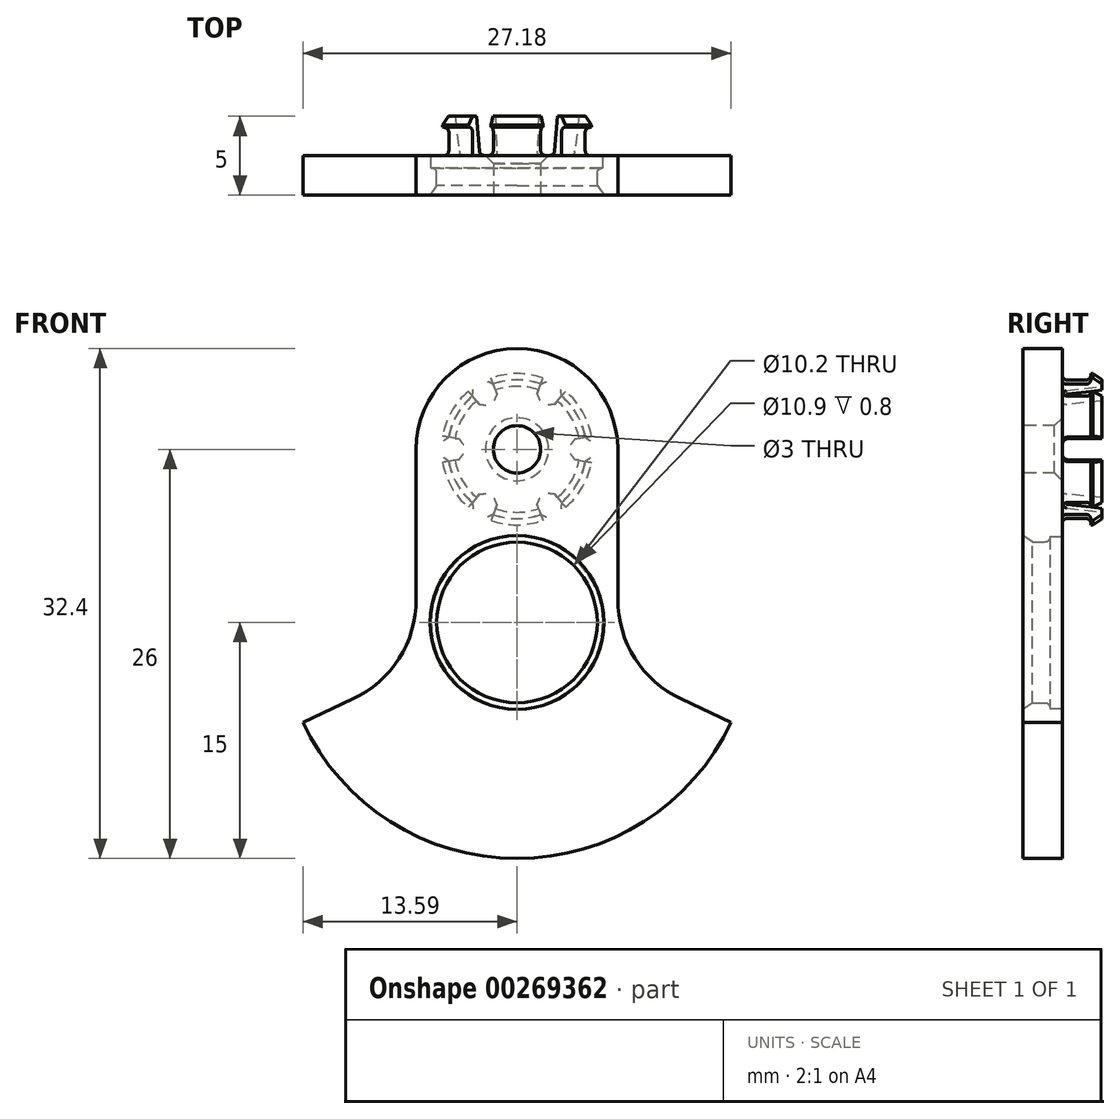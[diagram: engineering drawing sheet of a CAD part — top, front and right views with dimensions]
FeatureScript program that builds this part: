
annotation { "Feature Type Name" : "Feature", "Feature Type Description" : "" }
export const myFeature = defineFeature(function(context is Context, id is Id, definition is map)
    precondition{}
    {
        {
            var Q0;
            Q0=qCreatedBy(makeId("Front.planeOp"),FACE);
            var sketch = newSketch(context, id + "F0", { "sketchPlane" : qUnion([Q0])});
            skCircle(sketch, "E0", {"center": v(0, 0) * mm, "radius": 4.4 * mm});
            skLineSegment(sketch, "E1", {"start": v(0, 0) * mm, "end": v(0, 25.39) * mm, "construction": true});
            skCircle(sketch, "E2", {"center": v(0, -11) * mm, "radius": 5.1 * mm});
            skArc(sketch, "E3", {"start": v(-13.6, -17.34) * mm, "mid": v(0, -26) * mm, "end": v(13.6, -17.34) * mm});
            skLineSegment(sketch, "E4", {"start": v(-10.44, -15.87) * mm, "end": v(-13.6, -17.34) * mm});
            skLineSegment(sketch, "E5", {"start": v(-13.6, -17.34) * mm, "end": v(-10.44, -15.87) * mm});
            skLineSegment(sketch, "E6", {"start": v(13.6, -17.34) * mm, "end": v(10.44, -15.87) * mm});
            skLineSegment(sketch, "E7", {"start": v(-6.4, 0) * mm, "end": v(-6.4, -9.52) * mm});
            skArc(sketch, "E8", {"start": v(-10.44, -15.87) * mm, "mid": v(-7.5, -13.29) * mm, "end": v(-6.4, -9.52) * mm});
            skLineSegment(sketch, "E9", {"start": v(6.4, 0) * mm, "end": v(6.4, -9.52) * mm});
            skArc(sketch, "E10", {"start": v(6.4, -9.52) * mm, "mid": v(7.5, -13.29) * mm, "end": v(10.44, -15.87) * mm});
            skArc(sketch, "E11.trimOffspring", {"start": v(6.4, 0) * mm, "mid": v(0, 6.4) * mm, "end": v(-6.4, 0) * mm});
            skSolve(sketch);
        }
        {
            var Q0;
            Q0=makeQuery(id+"F0.imprint","IMPRINT",FACE,{"disambiguationData":[TD([[makeQuery(id+"F0.imprint","IMPRINT",EDGE,{"derivedFrom":sQuery(id+"F0.wireOp",EDGE,"E0")}),-1.0]])]});
            var Q1;
            Q1=makeQuery(id+"F0.imprint","IMPRINT",FACE,{"disambiguationData":[TD([[makeQuery(id+"F0.imprint","IMPRINT",EDGE,{"derivedFrom":sQuery(id+"F0.wireOp",EDGE,"E0")}),1.0]])]});
            extrude(context, id + "F1", {"entities" : qUnion([Q0, Q1]), "depth" : 2.5 * mm});
        }
        {
            var Q0;
            Q0=qCreatedBy(makeId("Top.planeOp"),FACE);
            cPlane(context, id + "F2", {"entities" : qUnion([Q0]), "cplaneType" : CPlaneType.OFFSET, "offset" : 11 * mm, "oppositeDirection" : true, "width" : 150 * mm, "height" : 150 * mm});
        }
        {
            var Q0;
            Q0=qCreatedBy(id+"F2.planeOp",FACE);
            var sketch = newSketch(context, id + "F3", { "sketchPlane" : qUnion([Q0])});
            skLineSegment(sketch, "E12.bottom", {"start": v(5, -0.8) * mm, "end": v(5.45, -0.8) * mm});
            skLineSegment(sketch, "E12.top", {"start": v(5, 0) * mm, "end": v(5.45, 0) * mm});
            skLineSegment(sketch, "E12.left", {"start": v(5, -0.8) * mm, "end": v(5, 0) * mm});
            skLineSegment(sketch, "E12.right", {"start": v(5.45, -0.8) * mm, "end": v(5.45, 0) * mm});
            skLineSegment(sketch, "E13", {"start": v(0, 0) * mm, "end": v(0, 6.8) * mm, "construction": true});
            skSolve(sketch);
        }
        {
            var Q0;
            Q0=makeQuery(id+"F3.imprint","IMPRINT",FACE,{"disambiguationData":[TD([[makeQuery(id+"F3.imprint","IMPRINT",EDGE,{"derivedFrom":sQuery(id+"F3.wireOp",EDGE,"E12.bottom")}),1.0]])]});
            var Q1;
            Q1=sQuery(id+"F3.wireOp",EDGE,"E13");
            revolve(context, id + "F4", {"operationType" : NewBodyOperationType.REMOVE, "entities" : qUnion([Q0]), "axis" : qUnion([Q1]), "revolveType" : RevolveType.FULL, "oppositeDirection" : true});
        }
        {
            var Q0;
            Q0=makeQuery(id+"F1.opExtrude","CAP_EDGE",EDGE,{"disambiguationData":[OSD([sQuery(id+"F0.wireOp",EDGE,"E2")])],"isStart":false});
            chamfer(context, id + "F5", {"entities" : qUnion([Q0]), "chamferType" : ChamferType.OFFSET_ANGLE, "width" : 0.6 * mm, "oppositeDirection" : false, "angle" : 35 * degree, "tangentPropagation" : true});
        }
        {
            var Q0;
            Q0=makeQuery(id+"F4.boolean.opBoolean","INTERSECT",EDGE,{"derivedFrom":[makeQuery(id+"F1.opExtrude","SWEPT_FACE",FACE,{"disambiguationData":[OSD([sQuery(id+"F0.wireOp",EDGE,"E2")])]}),makeQuery(id+"F4.opRevolve","SWEPT_FACE",FACE,{"disambiguationData":[OSD([sQuery(id+"F3.wireOp",EDGE,"E12.bottom")])]})]});
            fillet(context, id + "F6", {"entities" : qUnion([Q0]), "radius" : 0.3 * mm, "tangentPropagation" : true, "allowEdgeOverflow" : false});
        }
        {
            var Q0;
            Q0=qCreatedBy(makeId("Top.planeOp"),FACE);
            var sketch = newSketch(context, id + "F7", { "sketchPlane" : qUnion([Q0])});
            skLineSegment(sketch, "E14.bottom", {"start": v(3.5, -2.5) * mm, "end": v(4.4, -2.5) * mm});
            skLineSegment(sketch, "E14.top", {"start": v(3.5, 2.5) * mm, "end": v(4.4, 2.5) * mm});
            skLineSegment(sketch, "E14.left", {"start": v(3.5, -2.5) * mm, "end": v(3.5, 2.5) * mm});
            skLineSegment(sketch, "E14.right", {"start": v(4.4, -2.5) * mm, "end": v(4.4, 1.8) * mm});
            skLineSegment(sketch, "E15", {"start": v(0, 0) * mm, "end": v(0, 10.72) * mm, "construction": true});
            skLineSegment(sketch, "E16.bottom", {"start": v(4.4, 2.5) * mm, "end": v(4.8, 2.5) * mm});
            skLineSegment(sketch, "E16.top", {"start": v(4.4, 1.8) * mm, "end": v(4.8, 1.8) * mm});
            skLineSegment(sketch, "E16.right", {"start": v(4.8, 2.5) * mm, "end": v(4.8, 1.8) * mm});
            skSolve(sketch);
        }
        {
            var Q0;
            Q0=makeQuery(id+"F7.imprint","IMPRINT",FACE,{"disambiguationData":[TD([[makeQuery(id+"F7.imprint","IMPRINT",EDGE,{"derivedFrom":sQuery(id+"F7.wireOp",EDGE,"E14.bottom")}),1.0]])]});
            var Q1;
            Q1=sQuery(id+"F7.wireOp",EDGE,"E15");
            revolve(context, id + "F8", {"operationType" : NewBodyOperationType.ADD, "entities" : qUnion([Q0]), "axis" : qUnion([Q1]), "revolveType" : RevolveType.FULL});
        }
        {
            var Q0;
            Q0=makeQuery(id+"F8.opRevolve","SWEPT_EDGE",EDGE,{"disambiguationData":[OSD([sQuery(id+"F7.wireOp",EDGE,"E14.right"),sQuery(id+"F7.wireOp",EDGE,"E16.top")])]});
            fillet(context, id + "F9", {"entities" : qUnion([Q0]), "radius" : 0.3 * mm, "tangentPropagation" : true, "allowEdgeOverflow" : false});
        }
        {
            var Q0;
            Q0=makeQuery(id+"F8.opRevolve","SWEPT_EDGE",EDGE,{"disambiguationData":[OSD([sQuery(id+"F7.wireOp",EDGE,"E14.top"),sQuery(id+"F7.wireOp",EDGE,"E14.left")])]});
            chamfer(context, id + "F10", {"entities" : qUnion([Q0]), "chamferType" : ChamferType.TWO_OFFSETS, "width1" : 0.5 * mm, "oppositeDirection" : false, "width2" : 4 * mm, "tangentPropagation" : true});
        }
        {
            var Q0;
            Q0=makeQuery(id+"F8.opRevolve","SWEPT_EDGE",EDGE,{"disambiguationData":[OSD([sQuery(id+"F7.wireOp",EDGE,"E16.bottom"),sQuery(id+"F7.wireOp",EDGE,"E16.right")])]});
            chamfer(context, id + "F11", {"entities" : qUnion([Q0]), "chamferType" : ChamferType.OFFSET_ANGLE, "width" : 0.55 * mm, "oppositeDirection" : false, "angle" : 35 * degree, "tangentPropagation" : true});
        }
        {
            var Q0;
            Q0=qCreatedBy(makeId("Front.planeOp"),FACE);
            var sketch = newSketch(context, id + "F12", { "sketchPlane" : qUnion([Q0])});
            skCircle(sketch, "E17", {"center": v(0, 0) * mm, "radius": 7.5 * mm});
            skLineSegment(sketch, "E18", {"start": v(0, 0) * mm, "end": v(0, 10.84) * mm, "construction": true});
            skLineSegment(sketch, "E19", {"start": v(0, 0) * mm, "end": v(-10.38, 0) * mm, "construction": true});
            skLineSegment(sketch, "E20", {"start": v(0, 0) * mm, "end": v(-2.57, 7.05) * mm});
            skLineSegment(sketch, "E21", {"start": v(0, 0) * mm, "end": v(-4.82, 5.75) * mm});
            skLineSegment(sketch, "E22.1.0", {"start": v(0, 0) * mm, "end": v(-7.39, 1.3) * mm});
            skLineSegment(sketch, "E22.1.1", {"start": v(0, 0) * mm, "end": v(-7.39, -1.3) * mm});
            skLineSegment(sketch, "E22.2.0", {"start": v(0, 0) * mm, "end": v(-4.82, -5.75) * mm});
            skLineSegment(sketch, "E22.2.1", {"start": v(0, 0) * mm, "end": v(-2.57, -7.05) * mm});
            skLineSegment(sketch, "E22.3.0", {"start": v(0, 0) * mm, "end": v(2.57, -7.05) * mm});
            skLineSegment(sketch, "E22.3.1", {"start": v(0, 0) * mm, "end": v(4.82, -5.75) * mm});
            skLineSegment(sketch, "E22.4.0", {"start": v(0, 0) * mm, "end": v(7.39, -1.3) * mm});
            skLineSegment(sketch, "E22.4.1", {"start": v(0, 0) * mm, "end": v(7.39, 1.3) * mm});
            skLineSegment(sketch, "E22.5.0", {"start": v(0, 0) * mm, "end": v(4.82, 5.75) * mm});
            skLineSegment(sketch, "E22.5.1", {"start": v(0, 0) * mm, "end": v(2.57, 7.05) * mm});
            skSolve(sketch);
        }
        {
            var Q0;
            {var subQ0=sQuery(id+"F12.wireOp",EDGE,"E22.5.0");Q0=makeQuery(id+"F12.imprint","IMPRINT",FACE,{"disambiguationData":[TD([[makeQuery(id+"F12.imprint","IMPRINT",EDGE,{"derivedFrom":subQ0}),1.0]])]});}
            var Q1;
            {var subQ0=sQuery(id+"F12.wireOp",EDGE,"E20");Q1=makeQuery(id+"F12.imprint","IMPRINT",FACE,{"disambiguationData":[TD([[makeQuery(id+"F12.imprint","IMPRINT",EDGE,{"derivedFrom":subQ0}),1.0]])]});}
            var Q2;
            {var subQ0=sQuery(id+"F12.wireOp",EDGE,"E22.4.0");Q2=makeQuery(id+"F12.imprint","IMPRINT",FACE,{"disambiguationData":[TD([[makeQuery(id+"F12.imprint","IMPRINT",EDGE,{"derivedFrom":subQ0}),1.0]])]});}
            var Q3;
            {var subQ0=sQuery(id+"F12.wireOp",EDGE,"E22.3.0");Q3=makeQuery(id+"F12.imprint","IMPRINT",FACE,{"disambiguationData":[TD([[makeQuery(id+"F12.imprint","IMPRINT",EDGE,{"derivedFrom":subQ0}),1.0]])]});}
            var Q4;
            {var subQ0=sQuery(id+"F12.wireOp",EDGE,"E22.2.0");Q4=makeQuery(id+"F12.imprint","IMPRINT",FACE,{"disambiguationData":[TD([[makeQuery(id+"F12.imprint","IMPRINT",EDGE,{"derivedFrom":subQ0}),1.0]])]});}
            var Q5;
            {var subQ0=sQuery(id+"F12.wireOp",EDGE,"E22.1.0");Q5=makeQuery(id+"F12.imprint","IMPRINT",FACE,{"disambiguationData":[TD([[makeQuery(id+"F12.imprint","IMPRINT",EDGE,{"derivedFrom":subQ0}),1.0]])]});}
            extrude(context, id + "F13", {"entities" : qUnion([Q0, Q1, Q2, Q3, Q4, Q5]), "operationType" : NewBodyOperationType.REMOVE, "endBound" : BoundingType.THROUGH_ALL, "oppositeDirection" : true, "depth" : 25 * mm});
        }
        {
            var Q0;
            Q0=makeQuery(id+"F13.boolean.opBoolean","COPY",EDGE,{"derivedFrom":makeQuery(id+"F13.opExtrude","CAP_EDGE",EDGE,{"disambiguationData":[OSD([sQuery(id+"F12.wireOp",EDGE,"E22.4.1")])],"isStart":true})});
            var Q1;
            Q1=makeQuery(id+"F13.boolean.opBoolean","COPY",EDGE,{"derivedFrom":makeQuery(id+"F13.opExtrude","CAP_EDGE",EDGE,{"disambiguationData":[OSD([sQuery(id+"F12.wireOp",EDGE,"E22.4.0")])],"isStart":true})});
            var Q2;
            Q2=makeQuery(id+"F13.boolean.opBoolean","COPY",EDGE,{"derivedFrom":makeQuery(id+"F13.opExtrude","CAP_EDGE",EDGE,{"disambiguationData":[OSD([sQuery(id+"F12.wireOp",EDGE,"E22.5.0")])],"isStart":true})});
            var Q3;
            Q3=makeQuery(id+"F13.boolean.opBoolean","COPY",EDGE,{"derivedFrom":makeQuery(id+"F13.opExtrude","CAP_EDGE",EDGE,{"disambiguationData":[OSD([sQuery(id+"F12.wireOp",EDGE,"E22.5.1")])],"isStart":true})});
            var Q4;
            Q4=makeQuery(id+"F13.boolean.opBoolean","COPY",EDGE,{"derivedFrom":makeQuery(id+"F13.opExtrude","CAP_EDGE",EDGE,{"disambiguationData":[OSD([sQuery(id+"F12.wireOp",EDGE,"E20")])],"isStart":true})});
            var Q5;
            Q5=makeQuery(id+"F13.boolean.opBoolean","COPY",EDGE,{"derivedFrom":makeQuery(id+"F13.opExtrude","CAP_EDGE",EDGE,{"disambiguationData":[OSD([sQuery(id+"F12.wireOp",EDGE,"E21")])],"isStart":true})});
            var Q6;
            Q6=makeQuery(id+"F13.boolean.opBoolean","COPY",EDGE,{"derivedFrom":makeQuery(id+"F13.opExtrude","CAP_EDGE",EDGE,{"disambiguationData":[OSD([sQuery(id+"F12.wireOp",EDGE,"E22.1.0")])],"isStart":true})});
            var Q7;
            Q7=makeQuery(id+"F13.boolean.opBoolean","COPY",EDGE,{"derivedFrom":makeQuery(id+"F13.opExtrude","CAP_EDGE",EDGE,{"disambiguationData":[OSD([sQuery(id+"F12.wireOp",EDGE,"E22.1.1")])],"isStart":true})});
            var Q8;
            Q8=makeQuery(id+"F13.boolean.opBoolean","COPY",EDGE,{"derivedFrom":makeQuery(id+"F13.opExtrude","CAP_EDGE",EDGE,{"disambiguationData":[OSD([sQuery(id+"F12.wireOp",EDGE,"E22.2.0")])],"isStart":true})});
            var Q9;
            Q9=makeQuery(id+"F13.boolean.opBoolean","COPY",EDGE,{"derivedFrom":makeQuery(id+"F13.opExtrude","CAP_EDGE",EDGE,{"disambiguationData":[OSD([sQuery(id+"F12.wireOp",EDGE,"E22.2.1")])],"isStart":true})});
            var Q10;
            Q10=makeQuery(id+"F13.boolean.opBoolean","COPY",EDGE,{"derivedFrom":makeQuery(id+"F13.opExtrude","CAP_EDGE",EDGE,{"disambiguationData":[OSD([sQuery(id+"F12.wireOp",EDGE,"E22.3.0")])],"isStart":true})});
            var Q11;
            Q11=makeQuery(id+"F13.boolean.opBoolean","COPY",EDGE,{"derivedFrom":makeQuery(id+"F13.opExtrude","CAP_EDGE",EDGE,{"disambiguationData":[OSD([sQuery(id+"F12.wireOp",EDGE,"E22.3.1")])],"isStart":true})});
            var Q12;
            {var subQ1=makeQuery(id+"F1.opExtrude","CAP_FACE",FACE,{"disambiguationData":[OSD([sQuery(id+"F0.wireOp",EDGE,"E2"),sQuery(id+"F0.wireOp",EDGE,"E3"),sQuery(id+"F0.wireOp",EDGE,"E5"),sQuery(id+"F0.wireOp",EDGE,"E6"),sQuery(id+"F0.wireOp",EDGE,"E7"),sQuery(id+"F0.wireOp",EDGE,"E8"),sQuery(id+"F0.wireOp",EDGE,"E9"),sQuery(id+"F0.wireOp",EDGE,"E10"),sQuery(id+"F0.wireOp",EDGE,"E11.trimOffspring")])],"isStart":true});var subQ2=makeQuery(id+"F8.opRevolve","SWEPT_FACE",FACE,{"disambiguationData":[OSD([sQuery(id+"F7.wireOp",EDGE,"E14.right")])]});var subQ3=sQuery(id+"F12.wireOp",EDGE,"E22.3.1");Q12=makeQuery(id+"F13.boolean.opBoolean","SPLIT",EDGE,{"disambiguationData":[TD([makeQuery(id+"F13.opExtrude","SWEPT_FACE",FACE,{"disambiguationData":[OSD([subQ3])]})])],"derivedFrom":makeQuery(id+"F8.boolean.opBoolean","INTERSECT",EDGE,{"derivedFrom":[subQ1,subQ2]})});}
            var Q13;
            {var subQ1=sQuery(id+"F7.wireOp",EDGE,"E14.left");var subQ2=sQuery(id+"F7.wireOp",EDGE,"E14.top");var subQ3=makeQuery(id+"F1.opExtrude","CAP_FACE",FACE,{"disambiguationData":[OSD([sQuery(id+"F0.wireOp",EDGE,"E2"),sQuery(id+"F0.wireOp",EDGE,"E3"),sQuery(id+"F0.wireOp",EDGE,"E5"),sQuery(id+"F0.wireOp",EDGE,"E6"),sQuery(id+"F0.wireOp",EDGE,"E7"),sQuery(id+"F0.wireOp",EDGE,"E8"),sQuery(id+"F0.wireOp",EDGE,"E9"),sQuery(id+"F0.wireOp",EDGE,"E10"),sQuery(id+"F0.wireOp",EDGE,"E11.trimOffspring")])],"isStart":true});var subQ4=sQuery(id+"F12.wireOp",EDGE,"E22.3.1");Q13=makeQuery(id+"F13.boolean.opBoolean","SPLIT",EDGE,{"disambiguationData":[TD([makeQuery(id+"F13.opExtrude","SWEPT_FACE",FACE,{"disambiguationData":[OSD([subQ4])]})])],"derivedFrom":makeQuery(id+"F10.opChamfer","BLEND_EDGE",EDGE,{"blendedFrom":[makeQuery(id+"F8.opRevolve","SWEPT_EDGE",EDGE,{"disambiguationData":[OSD([subQ2,subQ1])]}),makeQuery(id+"F8.boolean.opBoolean","SPLIT",FACE,{"disambiguationData":[TD([makeQuery(id+"F8.opRevolve","SWEPT_FACE",FACE,{"disambiguationData":[OSD([subQ1])]})])],"derivedFrom":subQ3})],"blendedInto":[makeQuery(id+"F8.boolean.opBoolean","SPLIT",FACE,{"disambiguationData":[TD([makeQuery(id+"F8.opRevolve","SWEPT_FACE",FACE,{"disambiguationData":[OSD([subQ1])]})])],"derivedFrom":subQ3})]})});}
            var Q14;
            {var subQ1=sQuery(id+"F7.wireOp",EDGE,"E14.left");var subQ2=sQuery(id+"F7.wireOp",EDGE,"E14.top");var subQ4=makeQuery(id+"F1.opExtrude","CAP_FACE",FACE,{"disambiguationData":[OSD([sQuery(id+"F0.wireOp",EDGE,"E2"),sQuery(id+"F0.wireOp",EDGE,"E3"),sQuery(id+"F0.wireOp",EDGE,"E5"),sQuery(id+"F0.wireOp",EDGE,"E6"),sQuery(id+"F0.wireOp",EDGE,"E7"),sQuery(id+"F0.wireOp",EDGE,"E8"),sQuery(id+"F0.wireOp",EDGE,"E9"),sQuery(id+"F0.wireOp",EDGE,"E10"),sQuery(id+"F0.wireOp",EDGE,"E11.trimOffspring")])],"isStart":true});var subQ5=sQuery(id+"F12.wireOp",EDGE,"E22.4.1");Q14=makeQuery(id+"F13.boolean.opBoolean","SPLIT",EDGE,{"disambiguationData":[TD([makeQuery(id+"F13.opExtrude","SWEPT_FACE",FACE,{"disambiguationData":[OSD([subQ5])]})])],"derivedFrom":makeQuery(id+"F10.opChamfer","BLEND_EDGE",EDGE,{"blendedFrom":[makeQuery(id+"F8.opRevolve","SWEPT_EDGE",EDGE,{"disambiguationData":[OSD([subQ2,subQ1])]}),makeQuery(id+"F8.boolean.opBoolean","SPLIT",FACE,{"disambiguationData":[TD([makeQuery(id+"F8.opRevolve","SWEPT_FACE",FACE,{"disambiguationData":[OSD([subQ1])]})])],"derivedFrom":subQ4})],"blendedInto":[makeQuery(id+"F8.boolean.opBoolean","SPLIT",FACE,{"disambiguationData":[TD([makeQuery(id+"F8.opRevolve","SWEPT_FACE",FACE,{"disambiguationData":[OSD([subQ1])]})])],"derivedFrom":subQ4})]})});}
            var Q15;
            {var subQ0=sQuery(id+"F12.wireOp",EDGE,"E20");var subQ2=sQuery(id+"F7.wireOp",EDGE,"E14.left");var subQ3=sQuery(id+"F7.wireOp",EDGE,"E14.top");var subQ5=makeQuery(id+"F1.opExtrude","CAP_FACE",FACE,{"disambiguationData":[OSD([sQuery(id+"F0.wireOp",EDGE,"E2"),sQuery(id+"F0.wireOp",EDGE,"E3"),sQuery(id+"F0.wireOp",EDGE,"E5"),sQuery(id+"F0.wireOp",EDGE,"E6"),sQuery(id+"F0.wireOp",EDGE,"E7"),sQuery(id+"F0.wireOp",EDGE,"E8"),sQuery(id+"F0.wireOp",EDGE,"E9"),sQuery(id+"F0.wireOp",EDGE,"E10"),sQuery(id+"F0.wireOp",EDGE,"E11.trimOffspring")])],"isStart":true});Q15=makeQuery(id+"F13.boolean.opBoolean","SPLIT",EDGE,{"disambiguationData":[TD([makeQuery(id+"F13.opExtrude","SWEPT_FACE",FACE,{"disambiguationData":[OSD([subQ0])]})])],"derivedFrom":makeQuery(id+"F10.opChamfer","BLEND_EDGE",EDGE,{"blendedFrom":[makeQuery(id+"F8.opRevolve","SWEPT_EDGE",EDGE,{"disambiguationData":[OSD([subQ3,subQ2])]}),makeQuery(id+"F8.boolean.opBoolean","SPLIT",FACE,{"disambiguationData":[TD([makeQuery(id+"F8.opRevolve","SWEPT_FACE",FACE,{"disambiguationData":[OSD([subQ2])]})])],"derivedFrom":subQ5})],"blendedInto":[makeQuery(id+"F8.boolean.opBoolean","SPLIT",FACE,{"disambiguationData":[TD([makeQuery(id+"F8.opRevolve","SWEPT_FACE",FACE,{"disambiguationData":[OSD([subQ2])]})])],"derivedFrom":subQ5})]})});}
            var Q16;
            {var subQ0=sQuery(id+"F12.wireOp",EDGE,"E21");var subQ2=sQuery(id+"F7.wireOp",EDGE,"E14.left");var subQ3=sQuery(id+"F7.wireOp",EDGE,"E14.top");var subQ4=makeQuery(id+"F1.opExtrude","CAP_FACE",FACE,{"disambiguationData":[OSD([sQuery(id+"F0.wireOp",EDGE,"E2"),sQuery(id+"F0.wireOp",EDGE,"E3"),sQuery(id+"F0.wireOp",EDGE,"E5"),sQuery(id+"F0.wireOp",EDGE,"E6"),sQuery(id+"F0.wireOp",EDGE,"E7"),sQuery(id+"F0.wireOp",EDGE,"E8"),sQuery(id+"F0.wireOp",EDGE,"E9"),sQuery(id+"F0.wireOp",EDGE,"E10"),sQuery(id+"F0.wireOp",EDGE,"E11.trimOffspring")])],"isStart":true});Q16=makeQuery(id+"F13.boolean.opBoolean","SPLIT",EDGE,{"disambiguationData":[TD([makeQuery(id+"F13.opExtrude","SWEPT_FACE",FACE,{"disambiguationData":[OSD([subQ0])]})])],"derivedFrom":makeQuery(id+"F10.opChamfer","BLEND_EDGE",EDGE,{"blendedFrom":[makeQuery(id+"F8.opRevolve","SWEPT_EDGE",EDGE,{"disambiguationData":[OSD([subQ3,subQ2])]}),makeQuery(id+"F8.boolean.opBoolean","SPLIT",FACE,{"disambiguationData":[TD([makeQuery(id+"F8.opRevolve","SWEPT_FACE",FACE,{"disambiguationData":[OSD([subQ2])]})])],"derivedFrom":subQ4})],"blendedInto":[makeQuery(id+"F8.boolean.opBoolean","SPLIT",FACE,{"disambiguationData":[TD([makeQuery(id+"F8.opRevolve","SWEPT_FACE",FACE,{"disambiguationData":[OSD([subQ2])]})])],"derivedFrom":subQ4})]})});}
            var Q17;
            {var subQ1=sQuery(id+"F7.wireOp",EDGE,"E14.left");var subQ2=sQuery(id+"F7.wireOp",EDGE,"E14.top");var subQ3=makeQuery(id+"F1.opExtrude","CAP_FACE",FACE,{"disambiguationData":[OSD([sQuery(id+"F0.wireOp",EDGE,"E2"),sQuery(id+"F0.wireOp",EDGE,"E3"),sQuery(id+"F0.wireOp",EDGE,"E5"),sQuery(id+"F0.wireOp",EDGE,"E6"),sQuery(id+"F0.wireOp",EDGE,"E7"),sQuery(id+"F0.wireOp",EDGE,"E8"),sQuery(id+"F0.wireOp",EDGE,"E9"),sQuery(id+"F0.wireOp",EDGE,"E10"),sQuery(id+"F0.wireOp",EDGE,"E11.trimOffspring")])],"isStart":true});var subQ5=sQuery(id+"F12.wireOp",EDGE,"E22.1.1");Q17=makeQuery(id+"F13.boolean.opBoolean","SPLIT",EDGE,{"disambiguationData":[TD([makeQuery(id+"F13.opExtrude","SWEPT_FACE",FACE,{"disambiguationData":[OSD([subQ5])]})])],"derivedFrom":makeQuery(id+"F10.opChamfer","BLEND_EDGE",EDGE,{"blendedFrom":[makeQuery(id+"F8.opRevolve","SWEPT_EDGE",EDGE,{"disambiguationData":[OSD([subQ2,subQ1])]}),makeQuery(id+"F8.boolean.opBoolean","SPLIT",FACE,{"disambiguationData":[TD([makeQuery(id+"F8.opRevolve","SWEPT_FACE",FACE,{"disambiguationData":[OSD([subQ1])]})])],"derivedFrom":subQ3})],"blendedInto":[makeQuery(id+"F8.boolean.opBoolean","SPLIT",FACE,{"disambiguationData":[TD([makeQuery(id+"F8.opRevolve","SWEPT_FACE",FACE,{"disambiguationData":[OSD([subQ1])]})])],"derivedFrom":subQ3})]})});}
            var Q18;
            {var subQ1=sQuery(id+"F7.wireOp",EDGE,"E14.left");var subQ2=sQuery(id+"F7.wireOp",EDGE,"E14.top");var subQ3=makeQuery(id+"F1.opExtrude","CAP_FACE",FACE,{"disambiguationData":[OSD([sQuery(id+"F0.wireOp",EDGE,"E2"),sQuery(id+"F0.wireOp",EDGE,"E3"),sQuery(id+"F0.wireOp",EDGE,"E5"),sQuery(id+"F0.wireOp",EDGE,"E6"),sQuery(id+"F0.wireOp",EDGE,"E7"),sQuery(id+"F0.wireOp",EDGE,"E8"),sQuery(id+"F0.wireOp",EDGE,"E9"),sQuery(id+"F0.wireOp",EDGE,"E10"),sQuery(id+"F0.wireOp",EDGE,"E11.trimOffspring")])],"isStart":true});var subQ4=sQuery(id+"F12.wireOp",EDGE,"E22.2.1");Q18=makeQuery(id+"F13.boolean.opBoolean","SPLIT",EDGE,{"disambiguationData":[TD([makeQuery(id+"F13.opExtrude","SWEPT_FACE",FACE,{"disambiguationData":[OSD([subQ4])]})])],"derivedFrom":makeQuery(id+"F10.opChamfer","BLEND_EDGE",EDGE,{"blendedFrom":[makeQuery(id+"F8.opRevolve","SWEPT_EDGE",EDGE,{"disambiguationData":[OSD([subQ2,subQ1])]}),makeQuery(id+"F8.boolean.opBoolean","SPLIT",FACE,{"disambiguationData":[TD([makeQuery(id+"F8.opRevolve","SWEPT_FACE",FACE,{"disambiguationData":[OSD([subQ1])]})])],"derivedFrom":subQ3})],"blendedInto":[makeQuery(id+"F8.boolean.opBoolean","SPLIT",FACE,{"disambiguationData":[TD([makeQuery(id+"F8.opRevolve","SWEPT_FACE",FACE,{"disambiguationData":[OSD([subQ1])]})])],"derivedFrom":subQ3})]})});}
            var Q19;
            {var subQ1=makeQuery(id+"F1.opExtrude","CAP_FACE",FACE,{"disambiguationData":[OSD([sQuery(id+"F0.wireOp",EDGE,"E2"),sQuery(id+"F0.wireOp",EDGE,"E3"),sQuery(id+"F0.wireOp",EDGE,"E5"),sQuery(id+"F0.wireOp",EDGE,"E6"),sQuery(id+"F0.wireOp",EDGE,"E7"),sQuery(id+"F0.wireOp",EDGE,"E8"),sQuery(id+"F0.wireOp",EDGE,"E9"),sQuery(id+"F0.wireOp",EDGE,"E10"),sQuery(id+"F0.wireOp",EDGE,"E11.trimOffspring")])],"isStart":true});var subQ2=sQuery(id+"F12.wireOp",EDGE,"E22.2.1");var subQ3=makeQuery(id+"F8.opRevolve","SWEPT_FACE",FACE,{"disambiguationData":[OSD([sQuery(id+"F7.wireOp",EDGE,"E14.right")])]});Q19=makeQuery(id+"F13.boolean.opBoolean","SPLIT",EDGE,{"disambiguationData":[TD([makeQuery(id+"F13.opExtrude","SWEPT_FACE",FACE,{"disambiguationData":[OSD([subQ2])]})])],"derivedFrom":makeQuery(id+"F8.boolean.opBoolean","INTERSECT",EDGE,{"derivedFrom":[subQ1,subQ3]})});}
            var Q20;
            {var subQ1=makeQuery(id+"F1.opExtrude","CAP_FACE",FACE,{"disambiguationData":[OSD([sQuery(id+"F0.wireOp",EDGE,"E2"),sQuery(id+"F0.wireOp",EDGE,"E3"),sQuery(id+"F0.wireOp",EDGE,"E5"),sQuery(id+"F0.wireOp",EDGE,"E6"),sQuery(id+"F0.wireOp",EDGE,"E7"),sQuery(id+"F0.wireOp",EDGE,"E8"),sQuery(id+"F0.wireOp",EDGE,"E9"),sQuery(id+"F0.wireOp",EDGE,"E10"),sQuery(id+"F0.wireOp",EDGE,"E11.trimOffspring")])],"isStart":true});var subQ3=makeQuery(id+"F8.opRevolve","SWEPT_FACE",FACE,{"disambiguationData":[OSD([sQuery(id+"F7.wireOp",EDGE,"E14.right")])]});var subQ4=sQuery(id+"F12.wireOp",EDGE,"E22.1.1");Q20=makeQuery(id+"F13.boolean.opBoolean","SPLIT",EDGE,{"disambiguationData":[TD([makeQuery(id+"F13.opExtrude","SWEPT_FACE",FACE,{"disambiguationData":[OSD([subQ4])]})])],"derivedFrom":makeQuery(id+"F8.boolean.opBoolean","INTERSECT",EDGE,{"derivedFrom":[subQ1,subQ3]})});}
            var Q21;
            {var subQ1=makeQuery(id+"F1.opExtrude","CAP_FACE",FACE,{"disambiguationData":[OSD([sQuery(id+"F0.wireOp",EDGE,"E2"),sQuery(id+"F0.wireOp",EDGE,"E3"),sQuery(id+"F0.wireOp",EDGE,"E5"),sQuery(id+"F0.wireOp",EDGE,"E6"),sQuery(id+"F0.wireOp",EDGE,"E7"),sQuery(id+"F0.wireOp",EDGE,"E8"),sQuery(id+"F0.wireOp",EDGE,"E9"),sQuery(id+"F0.wireOp",EDGE,"E10"),sQuery(id+"F0.wireOp",EDGE,"E11.trimOffspring")])],"isStart":true});var subQ2=sQuery(id+"F12.wireOp",EDGE,"E21");var subQ3=makeQuery(id+"F8.opRevolve","SWEPT_FACE",FACE,{"disambiguationData":[OSD([sQuery(id+"F7.wireOp",EDGE,"E14.right")])]});Q21=makeQuery(id+"F13.boolean.opBoolean","SPLIT",EDGE,{"disambiguationData":[TD([makeQuery(id+"F13.opExtrude","SWEPT_FACE",FACE,{"disambiguationData":[OSD([subQ2])]})])],"derivedFrom":makeQuery(id+"F8.boolean.opBoolean","INTERSECT",EDGE,{"derivedFrom":[subQ1,subQ3]})});}
            var Q22;
            {var subQ2=makeQuery(id+"F1.opExtrude","CAP_FACE",FACE,{"disambiguationData":[OSD([sQuery(id+"F0.wireOp",EDGE,"E2"),sQuery(id+"F0.wireOp",EDGE,"E3"),sQuery(id+"F0.wireOp",EDGE,"E5"),sQuery(id+"F0.wireOp",EDGE,"E6"),sQuery(id+"F0.wireOp",EDGE,"E7"),sQuery(id+"F0.wireOp",EDGE,"E8"),sQuery(id+"F0.wireOp",EDGE,"E9"),sQuery(id+"F0.wireOp",EDGE,"E10"),sQuery(id+"F0.wireOp",EDGE,"E11.trimOffspring")])],"isStart":true});var subQ3=sQuery(id+"F12.wireOp",EDGE,"E20");var subQ4=makeQuery(id+"F8.opRevolve","SWEPT_FACE",FACE,{"disambiguationData":[OSD([sQuery(id+"F7.wireOp",EDGE,"E14.right")])]});Q22=makeQuery(id+"F13.boolean.opBoolean","SPLIT",EDGE,{"disambiguationData":[TD([makeQuery(id+"F13.opExtrude","SWEPT_FACE",FACE,{"disambiguationData":[OSD([subQ3])]})])],"derivedFrom":makeQuery(id+"F8.boolean.opBoolean","INTERSECT",EDGE,{"derivedFrom":[subQ2,subQ4]})});}
            var Q23;
            {var subQ2=makeQuery(id+"F1.opExtrude","CAP_FACE",FACE,{"disambiguationData":[OSD([sQuery(id+"F0.wireOp",EDGE,"E2"),sQuery(id+"F0.wireOp",EDGE,"E3"),sQuery(id+"F0.wireOp",EDGE,"E5"),sQuery(id+"F0.wireOp",EDGE,"E6"),sQuery(id+"F0.wireOp",EDGE,"E7"),sQuery(id+"F0.wireOp",EDGE,"E8"),sQuery(id+"F0.wireOp",EDGE,"E9"),sQuery(id+"F0.wireOp",EDGE,"E10"),sQuery(id+"F0.wireOp",EDGE,"E11.trimOffspring")])],"isStart":true});var subQ3=makeQuery(id+"F8.opRevolve","SWEPT_FACE",FACE,{"disambiguationData":[OSD([sQuery(id+"F7.wireOp",EDGE,"E14.right")])]});var subQ4=sQuery(id+"F12.wireOp",EDGE,"E22.4.1");Q23=makeQuery(id+"F13.boolean.opBoolean","SPLIT",EDGE,{"disambiguationData":[TD([makeQuery(id+"F13.opExtrude","SWEPT_FACE",FACE,{"disambiguationData":[OSD([subQ4])]})])],"derivedFrom":makeQuery(id+"F8.boolean.opBoolean","INTERSECT",EDGE,{"derivedFrom":[subQ2,subQ3]})});}
            fillet(context, id + "F14", {"entities" : qUnion([Q0, Q1, Q2, Q3, Q4, Q5, Q6, Q7, Q8, Q9, Q10, Q11, Q12, Q13, Q14, Q15, Q16, Q17, Q18, Q19, Q20, Q21, Q22, Q23]), "radius" : 0.3 * mm, "tangentPropagation" : true, "allowEdgeOverflow" : false});
        }
        {
            var Q0;
            Q0=qCreatedBy(makeId("Top.planeOp"),FACE);
            var sketch = newSketch(context, id + "F15", { "sketchPlane" : qUnion([Q0])});
            skLineSegment(sketch, "E23", {"start": v(0, -2) * mm, "end": v(0, 59.52) * mm, "construction": true});
            skLineSegment(sketch, "E24.bottom", {"start": v(0, -2) * mm, "end": v(1.5, -2) * mm});
            skLineSegment(sketch, "E24.top", {"start": v(0, 8) * mm, "end": v(1.5, 8) * mm});
            skLineSegment(sketch, "E24.left", {"start": v(0, -2) * mm, "end": v(0, 8) * mm});
            skLineSegment(sketch, "E24.right", {"start": v(1.5, -2) * mm, "end": v(1.5, 8) * mm});
            skSolve(sketch);
        }
        {
            var Q0;
            Q0=qCreatedBy(makeId("Top.planeOp"),FACE);
            var sketch = newSketch(context, id + "F16", { "sketchPlane" : qUnion([Q0])});
            skLineSegment(sketch, "E25.bottom", {"start": v(0, 10) * mm, "end": v(1.5, 10) * mm});
            skLineSegment(sketch, "E25.top", {"start": v(0, -10) * mm, "end": v(1.5, -10) * mm});
            skLineSegment(sketch, "E25.left", {"start": v(0, 10) * mm, "end": v(0, -10) * mm});
            skLineSegment(sketch, "E25.right", {"start": v(1.5, 10) * mm, "end": v(1.5, -10) * mm});
            skSolve(sketch);
        }
        {
            var Q0;
            Q0=makeQuery(id+"F16.imprint","IMPRINT",FACE,{"disambiguationData":[TD([[makeQuery(id+"F16.imprint","IMPRINT",EDGE,{"derivedFrom":sQuery(id+"F16.wireOp",EDGE,"E25.bottom")}),-1.0]])]});
            var Q1;
            Q1=sQuery(id+"F16.wireOp",EDGE,"E25.left");
            revolve(context, id + "F17", {"operationType" : NewBodyOperationType.REMOVE, "entities" : qUnion([Q0]), "axis" : qUnion([Q1]), "revolveType" : RevolveType.FULL, "oppositeDirection" : true});
        }
        {
            var Q0;
            {var subQ0=sQuery(id+"F12.wireOp",EDGE,"E17");var subQ1=sQuery(id+"F0.wireOp",EDGE,"E11.trimOffspring");var subQ2=sQuery(id+"F0.wireOp",EDGE,"E10");var subQ3=sQuery(id+"F0.wireOp",EDGE,"E9");var subQ4=sQuery(id+"F0.wireOp",EDGE,"E8");var subQ5=sQuery(id+"F0.wireOp",EDGE,"E7");var subQ6=sQuery(id+"F0.wireOp",EDGE,"E6");var subQ7=sQuery(id+"F0.wireOp",EDGE,"E5");var subQ8=sQuery(id+"F0.wireOp",EDGE,"E3");var subQ9=makeQuery(id+"F1.opExtrude","CAP_FACE",FACE,{"disambiguationData":[OSD([sQuery(id+"F0.wireOp",EDGE,"E2"),subQ8,subQ7,subQ6,subQ5,subQ4,subQ3,subQ2,subQ1])],"isStart":true});Q0=makeQuery(id+"F17.boolean.opBoolean","INTERSECT",EDGE,{"derivedFrom":[makeQuery(id+"F13.boolean.opBoolean","MERGE",FACE,{"derivedFrom":[makeQuery(id+"F8.boolean.opBoolean","SPLIT",FACE,{"disambiguationData":[TD([makeQuery(id+"F1.opExtrude","SWEPT_FACE",FACE,{"disambiguationData":[OSD([subQ8])]})])],"derivedFrom":subQ9}),makeQuery(id+"F8.boolean.opBoolean","SPLIT",FACE,{"disambiguationData":[TD([makeQuery(id+"F8.opRevolve","SWEPT_FACE",FACE,{"disambiguationData":[OSD([sQuery(id+"F7.wireOp",EDGE,"E14.left")])]})])],"derivedFrom":subQ9}),makeQuery(id+"F13.opExtrude","CAP_FACE",FACE,{"disambiguationData":[OSD([subQ0,sQuery(id+"F12.wireOp",EDGE,"E22.5.0"),sQuery(id+"F12.wireOp",EDGE,"E22.5.1")])],"isStart":true}),makeQuery(id+"F13.opExtrude","CAP_FACE",FACE,{"disambiguationData":[OSD([subQ0,sQuery(id+"F12.wireOp",EDGE,"E20"),sQuery(id+"F12.wireOp",EDGE,"E21")])],"isStart":true}),makeQuery(id+"F13.opExtrude","CAP_FACE",FACE,{"disambiguationData":[OSD([subQ0,sQuery(id+"F12.wireOp",EDGE,"E22.1.0"),sQuery(id+"F12.wireOp",EDGE,"E22.1.1")])],"isStart":true}),makeQuery(id+"F13.opExtrude","CAP_FACE",FACE,{"disambiguationData":[OSD([subQ0,sQuery(id+"F12.wireOp",EDGE,"E22.2.0"),sQuery(id+"F12.wireOp",EDGE,"E22.2.1")])],"isStart":true}),makeQuery(id+"F13.opExtrude","CAP_FACE",FACE,{"disambiguationData":[OSD([subQ0,sQuery(id+"F12.wireOp",EDGE,"E22.3.0"),sQuery(id+"F12.wireOp",EDGE,"E22.3.1")])],"isStart":true}),makeQuery(id+"F13.opExtrude","CAP_FACE",FACE,{"disambiguationData":[OSD([subQ0,sQuery(id+"F12.wireOp",EDGE,"E22.4.0"),sQuery(id+"F12.wireOp",EDGE,"E22.4.1")])],"isStart":true})]}),makeQuery(id+"F17.opRevolve","SWEPT_FACE",FACE,{"disambiguationData":[OSD([sQuery(id+"F16.wireOp",EDGE,"E25.right")])]})]});}
            chamfer(context, id + "F18", {"entities" : qUnion([Q0]), "width" : 0.5 * mm, "tangentPropagation" : true});
        }
    });
